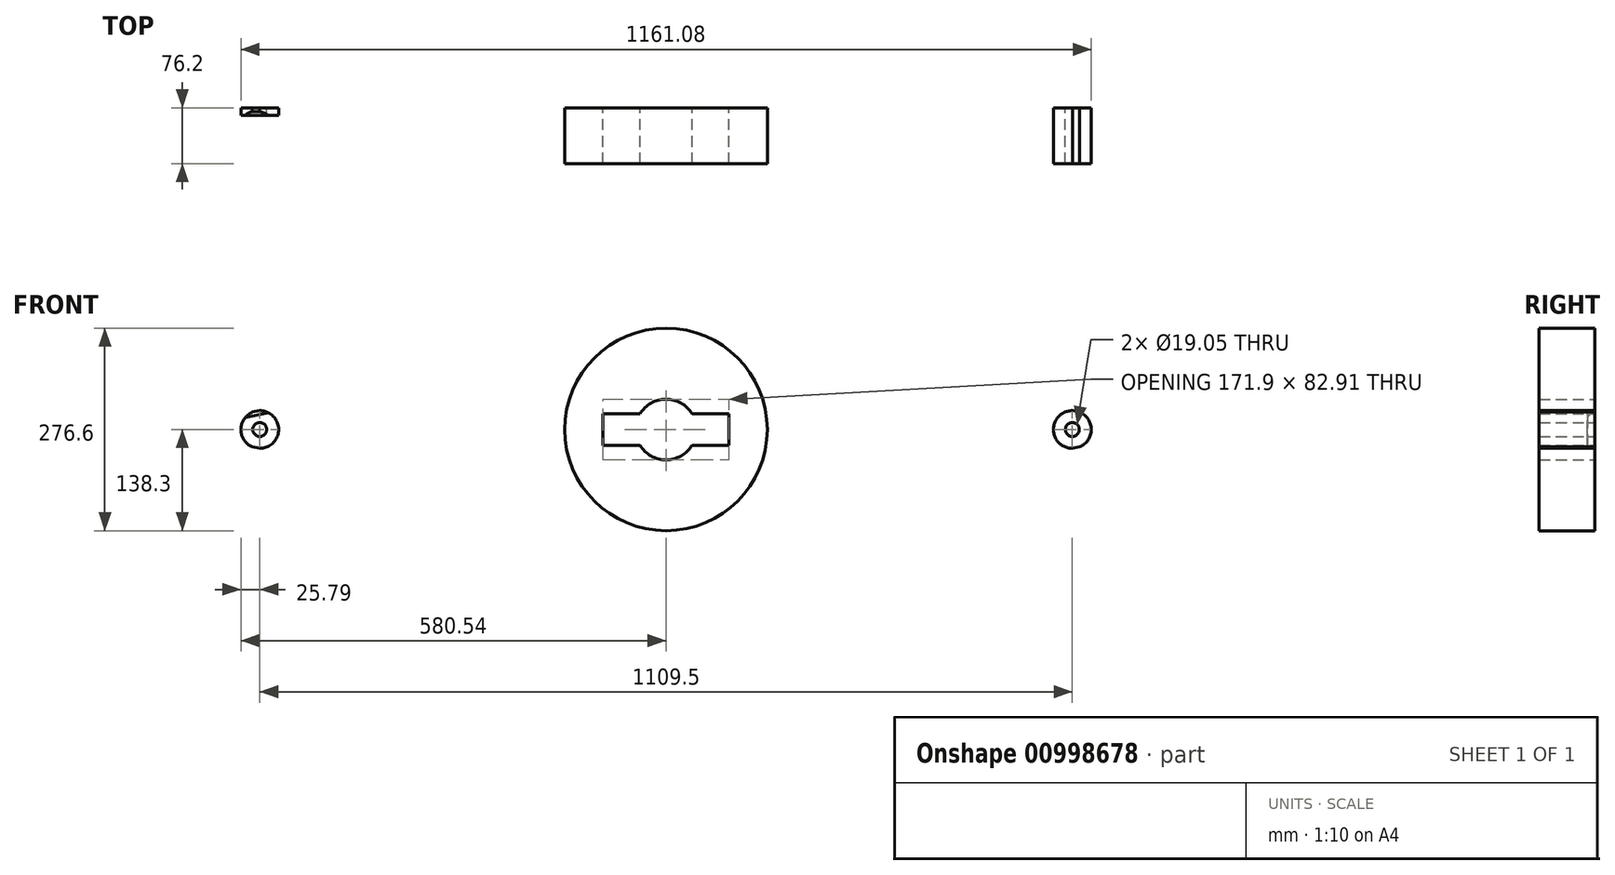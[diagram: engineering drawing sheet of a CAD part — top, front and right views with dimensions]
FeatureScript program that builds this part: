
annotation { "Feature Type Name" : "Feature", "Feature Type Description" : "" }
export const myFeature = defineFeature(function(context is Context, id is Id, definition is map)
    precondition{}
    {
        {
            var Q0;
            Q0=qCreatedBy(makeId("Front.planeOp"),FACE);
            var sketch = newSketch(context, id + "F0", { "sketchPlane" : qUnion([Q0])});
            skCircle(sketch, "E0", {"center": v(0, 0) * mm, "radius": 138.3 * mm});
            skCircle(sketch, "E1", {"center": v(0, 0) * mm, "radius": 41.46 * mm});
            skCircle(sketch, "E2", {"center": v(-554.75, 0) * mm, "radius": 25.79 * mm});
            skCircle(sketch, "E3", {"center": v(554.75, 0) * mm, "radius": 25.79 * mm});
            skLineSegment(sketch, "E4", {"start": v(-564.75, -23.77) * mm, "end": v(-28.17, -135.4) * mm});
            skLineSegment(sketch, "E5", {"start": v(564.75, -23.77) * mm, "end": v(28.17, -135.4) * mm});
            skLineSegment(sketch, "E6", {"start": v(564.86, 23.72) * mm, "end": v(28.17, 135.4) * mm});
            skLineSegment(sketch, "E7", {"start": v(-564.86, 23.72) * mm, "end": v(-28.17, 135.4) * mm});
            skLineSegment(sketch, "E8", {"start": v(0, 0) * mm, "end": v(0, 354.74) * mm, "construction": true});
            skLineSegment(sketch, "E9.bottom", {"start": v(85.95, -21.49) * mm, "end": v(-85.95, -21.49) * mm});
            skLineSegment(sketch, "E9.top", {"start": v(85.95, 21.49) * mm, "end": v(-85.95, 21.49) * mm});
            skLineSegment(sketch, "E9.left", {"start": v(85.95, -21.49) * mm, "end": v(85.95, 21.49) * mm});
            skLineSegment(sketch, "E9.right", {"start": v(-85.95, -21.49) * mm, "end": v(-85.95, 21.49) * mm});
            skCircle(sketch, "E10", {"center": v(-554.75, 0) * mm, "radius": 9.53 * mm});
            skCircle(sketch, "E11", {"center": v(554.75, 0) * mm, "radius": 9.53 * mm});
            skSolve(sketch);
        }
        {
            var Q0;
            {var subQ5=sQuery(id+"F0.wireOp",EDGE,"E0");var subQ7=makeQuery(id+"F0.imprint","IMPRINT",VERTEX,{"derivedFrom":subQ5});Q0=makeQuery(id+"F0.imprint","IMPRINT",FACE,{"disambiguationData":[TD([[makeQuery(id+"F0.imprint","IMPRINT",EDGE,{"disambiguationData":[TD([[subQ7,1.0]])],"derivedFrom":subQ5}),-1.0]])]});}
            var Q1;
            {var subQ6=sQuery(id+"F0.wireOp",EDGE,"E9.left");Q1=makeQuery(id+"F0.imprint","IMPRINT",FACE,{"disambiguationData":[TD([[makeQuery(id+"F0.imprint","IMPRINT",EDGE,{"derivedFrom":subQ6}),-1.0]])]});}
            var Q2;
            Q2=makeQuery(id+"F0.imprint","IMPRINT",FACE,{"disambiguationData":[TD([[makeQuery(id+"F0.imprint","IMPRINT",EDGE,{"derivedFrom":sQuery(id+"F0.wireOp",EDGE,"E11")}),-1.0]])]});
            extrude(context, id + "F1", {"entities" : qUnion([Q0, Q1, Q2]), "depth" : 76.2 * mm, "offsetDistance" : 25.4 * mm});
        }
        {
            var Q0;
            {var subQ1=sQuery(id+"F0.wireOp",EDGE,"E2");var subQ5=makeQuery(id+"F0.imprint","IMPRINT",VERTEX,{"derivedFrom":subQ1});Q0=makeQuery(id+"F0.imprint","IMPRINT",FACE,{"disambiguationData":[TD([[makeQuery(id+"F0.imprint","IMPRINT",EDGE,{"disambiguationData":[TD([[subQ5,-1.0]])],"derivedFrom":subQ1}),-1.0]])]});}
            var Q1;
            Q1=makeQuery(id+"F0.imprint","IMPRINT",FACE,{"disambiguationData":[TD([[makeQuery(id+"F0.imprint","IMPRINT",EDGE,{"derivedFrom":sQuery(id+"F0.wireOp",EDGE,"E10")}),-1.0]])]});
            extrude(context, id + "F2", {"entities" : qUnion([Q0, Q1]), "operationType" : NewBodyOperationType.ADD, "depth" : 10.16 * mm, "offsetDistance" : 25.4 * mm});
        }
        {
            var Q0;
            Q0=makeQuery(id+"F2.opExtrude","CAP_EDGE",EDGE,{"disambiguationData":[OSD([sQuery(id+"F0.wireOp",EDGE,"E7")])],"isStart":false});
            chamfer(context, id + "F3", {"entities" : qUnion([Q0]), "width" : 5.08 * mm, "tangentPropagation" : true});
        }
    });
